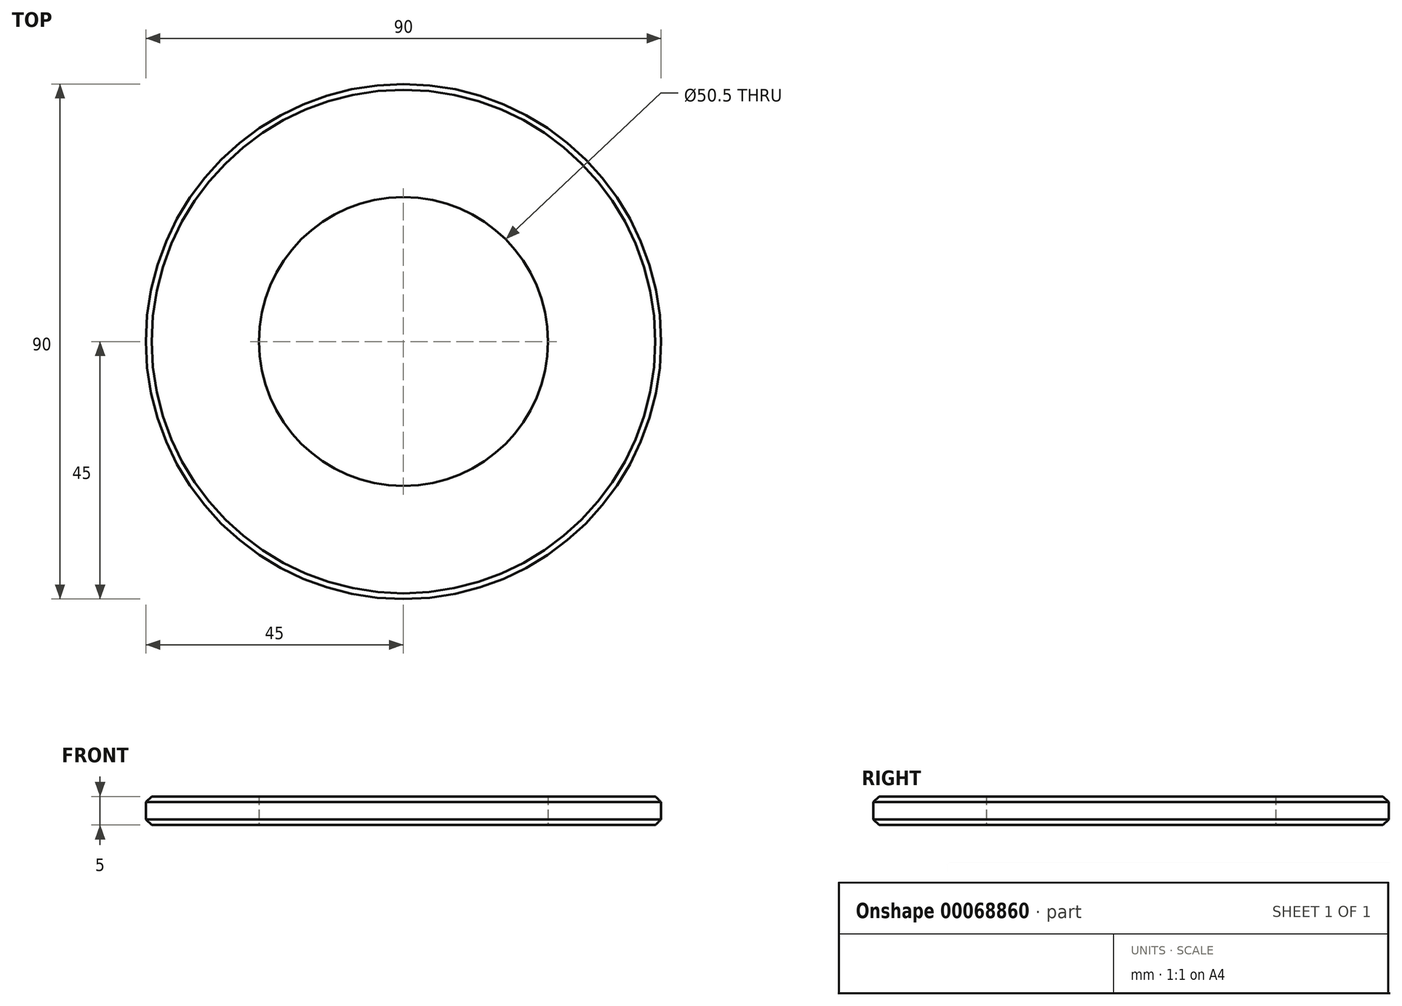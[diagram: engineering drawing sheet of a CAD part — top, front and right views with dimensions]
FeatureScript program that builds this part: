
annotation { "Feature Type Name" : "Feature", "Feature Type Description" : "" }
export const myFeature = defineFeature(function(context is Context, id is Id, definition is map)
    precondition{}
    {
        {
            var Q0;
            Q0=qCreatedBy(makeId("Top.planeOp"),FACE);
            var sketch = newSketch(context, id + "F0", { "sketchPlane" : qUnion([Q0])});
            skCircle(sketch, "E0", {"center": v(0, 0) * mm, "radius": 45 * mm});
            skCircle(sketch, "E1", {"center": v(0, 0) * mm, "radius": 25.25 * mm});
            skSolve(sketch);
        }
        {
            var Q0;
            Q0 = qSketchRegion(id + "F0", true);
            extrude(context, id + "F1", {"entities" : qUnion([Q0]), "endBound" : BoundingType.SYMMETRIC, "depth" : 5 * mm});
        }
        {
            var Q0;
            Q0=makeQuery(id+"F1.opExtrude","SWEPT_FACE",FACE,{"disambiguationData":[OSD([sQuery(id+"F0.wireOp",EDGE,"E0")])]});
            chamfer(context, id + "F2", {"entities" : qUnion([Q0]), "width" : 1 * mm, "tangentPropagation" : true});
        }
    });
